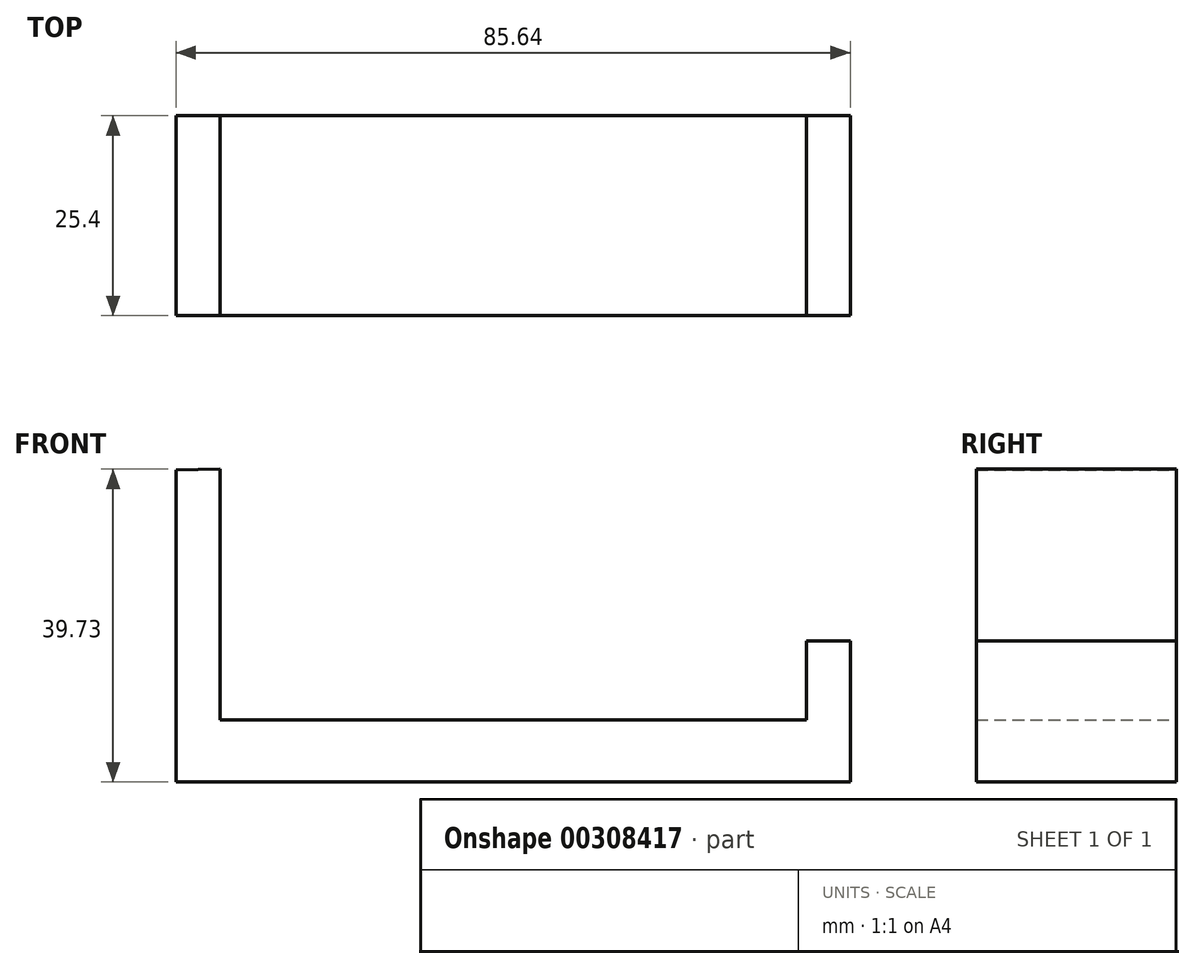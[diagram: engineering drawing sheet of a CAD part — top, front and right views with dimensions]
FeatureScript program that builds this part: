
annotation { "Feature Type Name" : "Feature", "Feature Type Description" : "" }
export const myFeature = defineFeature(function(context is Context, id is Id, definition is map)
    precondition{}
    {
        {
            var Q0;
            Q0=qCreatedBy(makeId("Front.planeOp"),FACE);
            var sketch = newSketch(context, id + "F0", { "sketchPlane" : qUnion([Q0])});
            skLineSegment(sketch, "E0", {"start": v(-17.7, 0) * mm, "end": v(56.79, 0) * mm});
            skLineSegment(sketch, "E1", {"start": v(-17.7, 0) * mm, "end": v(-17.7, 31.86) * mm});
            skLineSegment(sketch, "E2", {"start": v(56.79, 0) * mm, "end": v(56.79, 10.05) * mm});
            skLineSegment(sketch, "E3", {"start": v(-23.27, -7.87) * mm, "end": v(62.37, -7.87) * mm});
            skLineSegment(sketch, "E4", {"start": v(-23.27, -7.87) * mm, "end": v(-23.27, 31.73) * mm});
            skLineSegment(sketch, "E5", {"start": v(-23.27, 31.73) * mm, "end": v(-17.7, 31.86) * mm});
            skLineSegment(sketch, "E6", {"start": v(56.79, 10.05) * mm, "end": v(62.37, 10.05) * mm});
            skLineSegment(sketch, "E7", {"start": v(62.37, 10.05) * mm, "end": v(62.37, -7.87) * mm});
            skSolve(sketch);
        }
        {
            var Q0;
            Q0=makeQuery(id+"F0.imprint","IMPRINT",FACE,{"disambiguationData":[TD([[makeQuery(id+"F0.imprint","IMPRINT",EDGE,{"derivedFrom":sQuery(id+"F0.wireOp",EDGE,"E0")}),-1.0]])]});
            extrude(context, id + "F1", {"entities" : qUnion([Q0]), "depth" : 25.4 * mm});
        }
    });
